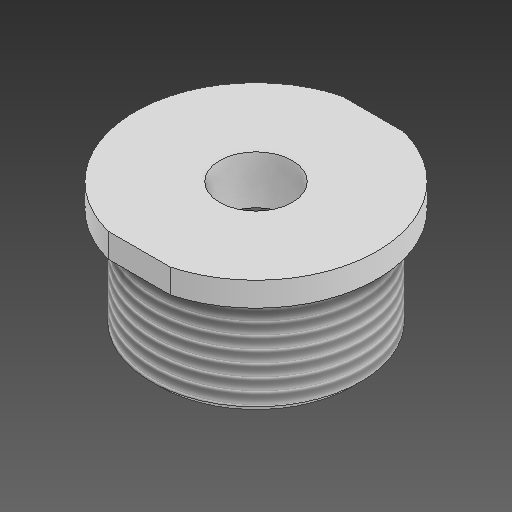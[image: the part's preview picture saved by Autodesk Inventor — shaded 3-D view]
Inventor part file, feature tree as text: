
AUTODESK INVENTOR PART (.ipt)
format: ipt  version: 2021 (Build 250183000, 183)  size: 183,808 bytes
history: native  units: mm
features: sketch x2, revolve x1, extrude x1, chamfer x1, thread x1
ambient origin geometry x8: Origin, YZ Plane, XZ Plane, XY Plane, X Axis, Y Axis, Z Axis, Center Point
bodies: Solid1 (feature_tree)
feature tree (6):
  revolve  "Revolution1"  [1 undecoded]
  extrude  "Extrusion1"  Depth=1.5mm
  chamfer  "Chamfer1"  Distance=15.0mm
  thread  "Thread3"  [1 undecoded]
  sketch  "Sketch1"  dims[d1=4.5mm d2=8.0mm]
  sketch  "Sketch2"  dims[d3=13.0mm d4=1.5mm d6=15.0mm d8=90.0deg d10=10.0mm d11=0.0mm d15=0.5mm d16=2.0mm d17=45.0deg d19=2.0mm d20=4.5mm d21=8.0mm d22=2.5mm d25=5.0mm d26=1.0mm d29=14.5mm d44=6.0mm d45=0.0mm]
note: 2 required parameter values undecoded (feature->parameter linkage not recoverable at this tier; creation-order binding heuristic only, values carry confidence <= 0.55)